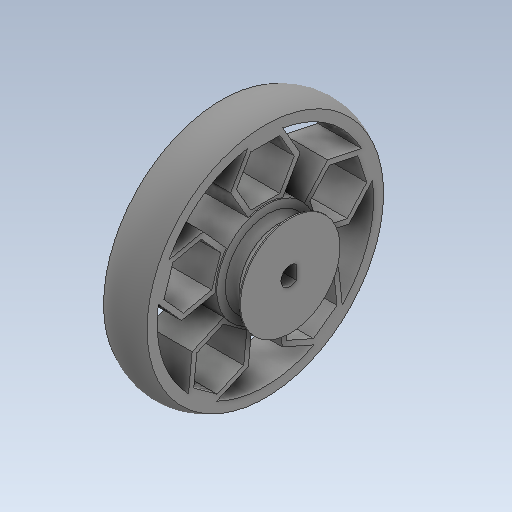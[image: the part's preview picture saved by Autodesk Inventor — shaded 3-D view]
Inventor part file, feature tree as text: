
AUTODESK INVENTOR PART (.ipt)
format: ipt  version: 2020 (Build 240168000, 168)  size: 425,984 bytes
history: native  units: in
note: dims shown in document units (in); Inventor stores cm internally (conversion verified against a paired STEP export)
features: sketch x4, extrude x2, revolve x2, projected_geometry x1
ambient origin geometry x8: Origin, YZ Plane, XZ Plane, XY Plane, X Axis, Y Axis, Z Axis, Center Point
bodies: Solid1 (feature_tree)
feature tree (9):
  extrude  "Extrusion1"  Depth=0.0394in
  sketch  "Sketch3"  dims[d6=0.6299in d7=0.1575in]
  revolve  "Revolution1"  [1 undecoded]
  extrude  "Extrusion2"  Depth=0.1575in
  revolve  "Revolution2"  [1 undecoded]
  sketch  "Sketch1"  dims[d0=0.1181in d1=0.0394in]
  sketch  "Sketch2"  dims[d3=1.4961in d4=0.1181in]
  projected_geometry  "Projected Loop1"
  sketch  "Sketch4"  dims[d8=0.0in d9=1.4961in d10=0.063in d11=0.0315in d16=0.2756in d17=0.0in d19=360.0deg d20=0.0787in d24=0.0394in d25=90.0deg d26=45.0deg d28=0.0079in d29=1.9685in d31=360.0deg]
note: 2 required parameter values undecoded (feature->parameter linkage not recoverable at this tier; creation-order binding heuristic only, values carry confidence <= 0.55)
